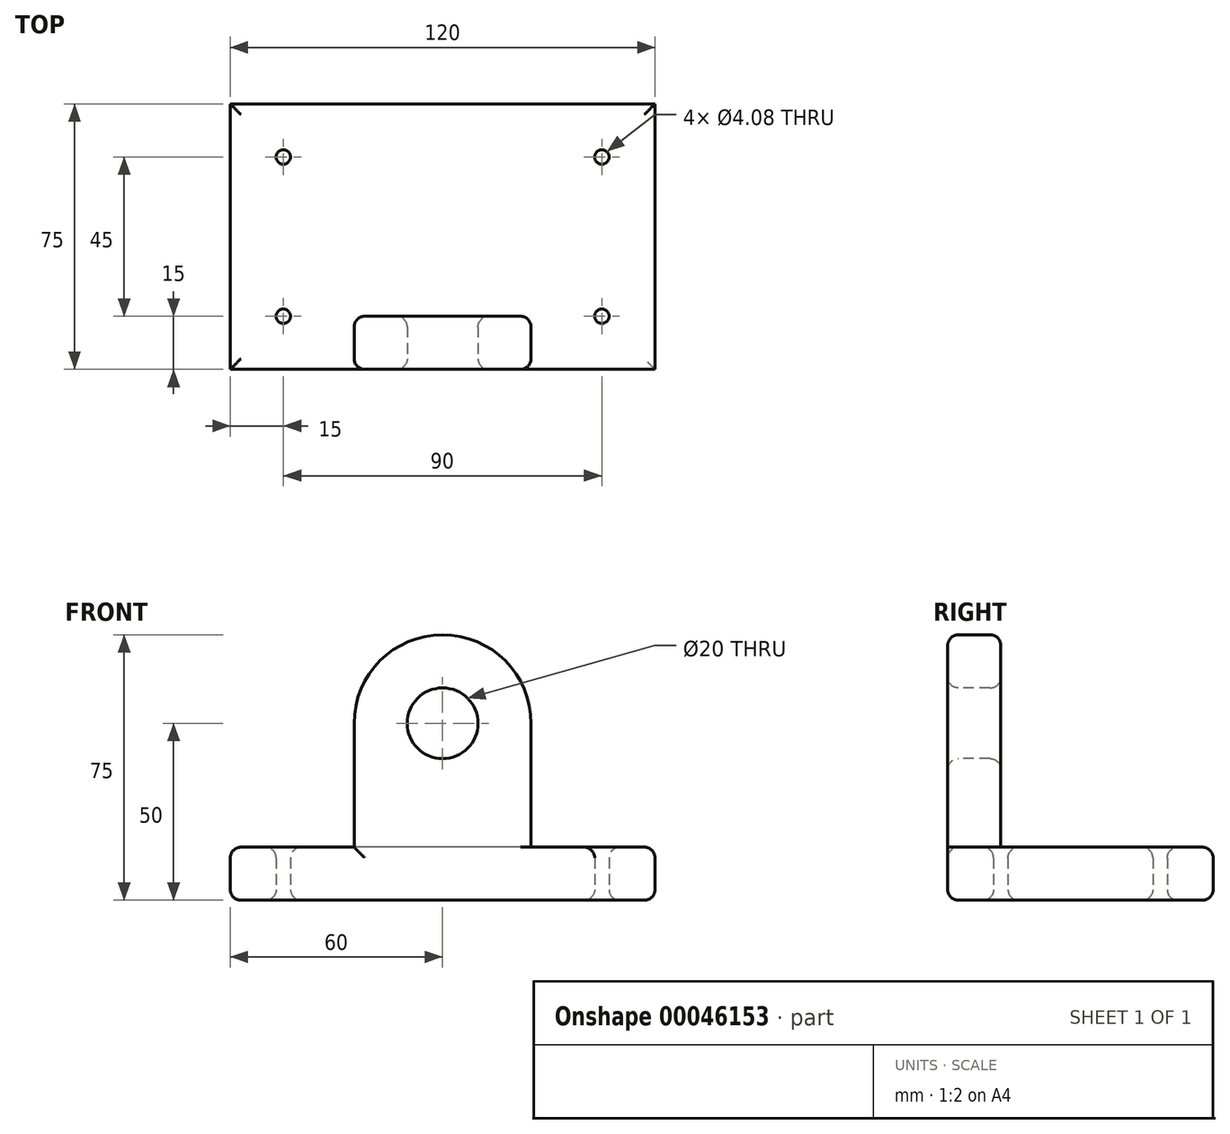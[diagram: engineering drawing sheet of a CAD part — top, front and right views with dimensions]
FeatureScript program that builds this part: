
annotation { "Feature Type Name" : "Feature", "Feature Type Description" : "" }
export const myFeature = defineFeature(function(context is Context, id is Id, definition is map)
    precondition{}
    {
        {
            var Q0;
            Q0=qCreatedBy(makeId("Top.planeOp"),FACE);
            var sketch = newSketch(context, id + "F0", { "sketchPlane" : qUnion([Q0])});
            skLineSegment(sketch, "E0.rect.bottom", {"start": v(60, -37.5) * mm, "end": v(-60, -37.5) * mm});
            skLineSegment(sketch, "E0.rect.top", {"start": v(60, 37.5) * mm, "end": v(-60, 37.5) * mm});
            skLineSegment(sketch, "E0.rect.left", {"start": v(60, -37.5) * mm, "end": v(60, 37.5) * mm});
            skLineSegment(sketch, "E0.rect.right", {"start": v(-60, -37.5) * mm, "end": v(-60, 37.5) * mm});
            skPoint(sketch, "E0.rect.middle", {"position": v(0, 0) * mm});
            skSolve(sketch);
        }
        {
            var Q0;
            Q0 = qSketchRegion(id + "F0", true);
            extrude(context, id + "F1", {"entities" : qUnion([Q0]), "depth" : 15 * mm});
        }
        {
            var Q0;
            Q0=makeQuery(id+"F1.opExtrude","SWEPT_FACE",FACE,{"disambiguationData":[OSD([sQuery(id+"F0.wireOp",EDGE,"E0.rect.bottom")])]});
            var sketch = newSketch(context, id + "F2", { "sketchPlane" : qUnion([Q0])});
            skLineSegment(sketch, "E1", {"start": v(0, 0) * mm, "end": v(0, 50) * mm, "construction": true});
            skCircle(sketch, "E2", {"center": v(0, 50) * mm, "radius": 25 * mm});
            skLineSegment(sketch, "E3", {"start": v(-25, 50) * mm, "end": v(-25, 0) * mm});
            skLineSegment(sketch, "E4", {"start": v(25, 50) * mm, "end": v(25, 0) * mm});
            skLineSegment(sketch, "E5", {"start": v(25, 0) * mm, "end": v(-25, 0) * mm});
            skCircle(sketch, "E6", {"center": v(0, 50) * mm, "radius": 10 * mm});
            skSolve(sketch);
        }
        {
            var Q0;
            {var subQ0=sQuery(id+"F2.wireOp",EDGE,"E2");var subQ2=makeQuery(id+"F2.imprint","INTERSECT",VERTEX,{"derivedFrom":[subQ0,sQuery(id+"F2.wireOp",EDGE,"E3")]});Q0=makeQuery(id+"F2.imprint","IMPRINT",FACE,{"disambiguationData":[TD([[makeQuery(id+"F2.imprint","IMPRINT",EDGE,{"disambiguationData":[TD([[subQ2,1.0]])],"derivedFrom":subQ0}),1.0]])]});}
            var Q1;
            {var subQ3=sQuery(id+"F2.wireOp",EDGE,"E3");var subQ5=sQuery(id+"F2.wireOp",EDGE,"E2");var subQ7=makeQuery(id+"F2.imprint","INTERSECT",VERTEX,{"derivedFrom":[subQ5,subQ3]});Q1=makeQuery(id+"F2.imprint","IMPRINT",FACE,{"disambiguationData":[TD([[makeQuery(id+"F2.imprint","IMPRINT",EDGE,{"disambiguationData":[TD([[subQ7,-1.0]])],"derivedFrom":subQ5}),-1.0]])]});}
            extrude(context, id + "F3", {"entities" : qUnion([Q0, Q1]), "operationType" : NewBodyOperationType.ADD, "oppositeDirection" : true, "depth" : 15 * mm});
        }
        {
            var Q0;
            Q0=qCreatedBy(makeId("Top.planeOp"),FACE);
            var sketch = newSketch(context, id + "F4", { "sketchPlane" : qUnion([Q0])});
            skLineSegment(sketch, "E7.rect.bottom", {"start": v(45, -22.5) * mm, "end": v(-45, -22.5) * mm, "construction": true});
            skLineSegment(sketch, "E7.rect.top", {"start": v(45, 22.5) * mm, "end": v(-45, 22.5) * mm, "construction": true});
            skLineSegment(sketch, "E7.rect.left", {"start": v(45, -22.5) * mm, "end": v(45, 22.5) * mm, "construction": true});
            skLineSegment(sketch, "E7.rect.right", {"start": v(-45, -22.5) * mm, "end": v(-45, 22.5) * mm, "construction": true});
            skPoint(sketch, "E7.rect.middle", {"position": v(0, 0) * mm});
            skCircle(sketch, "E8", {"center": v(-45, 22.5) * mm, "radius": 2.04 * mm});
            skCircle(sketch, "E9", {"center": v(45, 22.5) * mm, "radius": 2.04 * mm});
            skCircle(sketch, "E10", {"center": v(45, -22.5) * mm, "radius": 2.04 * mm});
            skCircle(sketch, "E11", {"center": v(-45, -22.5) * mm, "radius": 2.04 * mm});
            skSolve(sketch);
        }
        {
            var Q0;
            Q0=makeQuery(id+"F4.imprint","IMPRINT",FACE,{"disambiguationData":[TD([[makeQuery(id+"F4.imprint","IMPRINT",EDGE,{"derivedFrom":sQuery(id+"F4.wireOp",EDGE,"E9")}),1.0]])]});
            var Q1;
            Q1=makeQuery(id+"F4.imprint","IMPRINT",FACE,{"disambiguationData":[TD([[makeQuery(id+"F4.imprint","IMPRINT",EDGE,{"derivedFrom":sQuery(id+"F4.wireOp",EDGE,"E8")}),1.0]])]});
            var Q2;
            Q2=makeQuery(id+"F4.imprint","IMPRINT",FACE,{"disambiguationData":[TD([[makeQuery(id+"F4.imprint","IMPRINT",EDGE,{"derivedFrom":sQuery(id+"F4.wireOp",EDGE,"E11")}),1.0]])]});
            var Q3;
            Q3=makeQuery(id+"F4.imprint","IMPRINT",FACE,{"disambiguationData":[TD([[makeQuery(id+"F4.imprint","IMPRINT",EDGE,{"derivedFrom":sQuery(id+"F4.wireOp",EDGE,"E10")}),1.0]])]});
            var Q4;
            Q4=sQuery(id+"F4.wireOp",EDGE,"E8");
            extrude(context, id + "F5", {"entities" : qUnion([Q0, Q1, Q2, Q3]), "operationType" : NewBodyOperationType.REMOVE, "surfaceEntities" : qUnion([Q4]), "endBound" : BoundingType.THROUGH_ALL, "depth" : 25 * mm});
        }
        {
            var Q0;
            Q0=makeQuery(id+"F3.opExtrude","CAP_EDGE",EDGE,{"disambiguationData":[OSD([sQuery(id+"F2.wireOp",EDGE,"E2")])],"isStart":true});
            var Q1;
            Q1=makeQuery(id+"F3.opExtrude","CAP_EDGE",EDGE,{"disambiguationData":[OSD([sQuery(id+"F2.wireOp",EDGE,"E2")])],"isStart":false});
            var Q2;
            Q2=makeQuery(id+"F1.opExtrude","CAP_EDGE",EDGE,{"disambiguationData":[OSD([sQuery(id+"F0.wireOp",EDGE,"E0.rect.left")])],"isStart":false});
            var Q3;
            Q3=makeQuery(id+"F1.opExtrude","CAP_EDGE",EDGE,{"disambiguationData":[OSD([sQuery(id+"F0.wireOp",EDGE,"E0.rect.right")])],"isStart":false});
            var Q4;
            Q4=makeQuery(id+"F1.opExtrude","CAP_EDGE",EDGE,{"disambiguationData":[OSD([sQuery(id+"F0.wireOp",EDGE,"E0.rect.top")])],"isStart":false});
            var Q5;
            {var subQ0=sQuery(id+"F0.wireOp",EDGE,"E0.rect.bottom");var subQ2=sQuery(id+"F0.wireOp",EDGE,"E0.rect.right");Q5=makeQuery(id+"F3.boolean.opBoolean","SPLIT",EDGE,{"disambiguationData":[TD([makeQuery(id+"F1.opExtrude","SWEPT_FACE",FACE,{"disambiguationData":[OSD([subQ2])]})])],"derivedFrom":makeQuery(id+"F1.opExtrude","CAP_EDGE",EDGE,{"disambiguationData":[OSD([subQ0])],"isStart":false})});}
            var Q6;
            Q6=makeQuery(id+"F5.boolean.opBoolean","INTERSECT",EDGE,{"derivedFrom":[makeQuery(id+"F1.opExtrude","CAP_FACE",FACE,{"disambiguationData":[OSD([sQuery(id+"F0.wireOp",EDGE,"E0.rect.bottom"),sQuery(id+"F0.wireOp",EDGE,"E0.rect.top"),sQuery(id+"F0.wireOp",EDGE,"E0.rect.left"),sQuery(id+"F0.wireOp",EDGE,"E0.rect.right")])],"isStart":false}),makeQuery(id+"F5.opExtrude","SWEPT_FACE",FACE,{"disambiguationData":[OSD([sQuery(id+"F4.wireOp",EDGE,"E11")])]})]});
            var Q7;
            Q7=makeQuery(id+"F5.boolean.opBoolean","INTERSECT",EDGE,{"derivedFrom":[makeQuery(id+"F1.opExtrude","CAP_FACE",FACE,{"disambiguationData":[OSD([sQuery(id+"F0.wireOp",EDGE,"E0.rect.bottom"),sQuery(id+"F0.wireOp",EDGE,"E0.rect.top"),sQuery(id+"F0.wireOp",EDGE,"E0.rect.left"),sQuery(id+"F0.wireOp",EDGE,"E0.rect.right")])],"isStart":false}),makeQuery(id+"F5.opExtrude","SWEPT_FACE",FACE,{"disambiguationData":[OSD([sQuery(id+"F4.wireOp",EDGE,"E8")])]})]});
            var Q8;
            Q8=makeQuery(id+"F5.boolean.opBoolean","INTERSECT",EDGE,{"derivedFrom":[makeQuery(id+"F1.opExtrude","CAP_FACE",FACE,{"disambiguationData":[OSD([sQuery(id+"F0.wireOp",EDGE,"E0.rect.bottom"),sQuery(id+"F0.wireOp",EDGE,"E0.rect.top"),sQuery(id+"F0.wireOp",EDGE,"E0.rect.left"),sQuery(id+"F0.wireOp",EDGE,"E0.rect.right")])],"isStart":false}),makeQuery(id+"F5.opExtrude","SWEPT_FACE",FACE,{"disambiguationData":[OSD([sQuery(id+"F4.wireOp",EDGE,"E9")])]})]});
            var Q9;
            Q9=makeQuery(id+"F5.boolean.opBoolean","INTERSECT",EDGE,{"derivedFrom":[makeQuery(id+"F1.opExtrude","CAP_FACE",FACE,{"disambiguationData":[OSD([sQuery(id+"F0.wireOp",EDGE,"E0.rect.bottom"),sQuery(id+"F0.wireOp",EDGE,"E0.rect.top"),sQuery(id+"F0.wireOp",EDGE,"E0.rect.left"),sQuery(id+"F0.wireOp",EDGE,"E0.rect.right")])],"isStart":false}),makeQuery(id+"F5.opExtrude","SWEPT_FACE",FACE,{"disambiguationData":[OSD([sQuery(id+"F4.wireOp",EDGE,"E10")])]})]});
            var Q10;
            Q10=makeQuery(id+"F3.opExtrude","CAP_EDGE",EDGE,{"disambiguationData":[OSD([sQuery(id+"F2.wireOp",EDGE,"E3")])],"isStart":true});
            var Q11;
            Q11=makeQuery(id+"F3.opExtrude","CAP_EDGE",EDGE,{"disambiguationData":[OSD([sQuery(id+"F2.wireOp",EDGE,"E3")])],"isStart":false});
            var Q12;
            Q12=makeQuery(id+"F3.opExtrude","CAP_EDGE",EDGE,{"disambiguationData":[OSD([sQuery(id+"F2.wireOp",EDGE,"E4")])],"isStart":false});
            var Q13;
            Q13=makeQuery(id+"F3.opExtrude","CAP_EDGE",EDGE,{"disambiguationData":[OSD([sQuery(id+"F2.wireOp",EDGE,"E4")])],"isStart":true});
            var Q14;
            Q14=makeQuery(id+"F3.opExtrude","CAP_EDGE",EDGE,{"disambiguationData":[OSD([sQuery(id+"F2.wireOp",EDGE,"E6")])],"isStart":false});
            var Q15;
            Q15=makeQuery(id+"F3.opExtrude","CAP_EDGE",EDGE,{"disambiguationData":[OSD([sQuery(id+"F2.wireOp",EDGE,"E6")])],"isStart":true});
            var Q16;
            Q16=makeQuery(id+"F3.opExtrude","SWEPT_EDGE",EDGE,{"disambiguationData":[OSD([sQuery(id+"F0.wireOp",EDGE,"E0.rect.bottom"),sQuery(id+"F2.wireOp",EDGE,"E3")])]});
            var Q17;
            Q17=makeQuery(id+"F1.opExtrude","CAP_FACE",FACE,{"disambiguationData":[OSD([sQuery(id+"F0.wireOp",EDGE,"E0.rect.bottom"),sQuery(id+"F0.wireOp",EDGE,"E0.rect.top"),sQuery(id+"F0.wireOp",EDGE,"E0.rect.left"),sQuery(id+"F0.wireOp",EDGE,"E0.rect.right")])],"isStart":true});
            fillet(context, id + "F6", {"entities" : qUnion([Q0, Q1, Q2, Q3, Q4, Q5, Q6, Q7, Q8, Q9, Q10, Q11, Q12, Q13, Q14, Q15, Q16, Q17]), "radius" : 3 * mm, "tangentPropagation" : true, "allowEdgeOverflow" : false});
        }
    });
